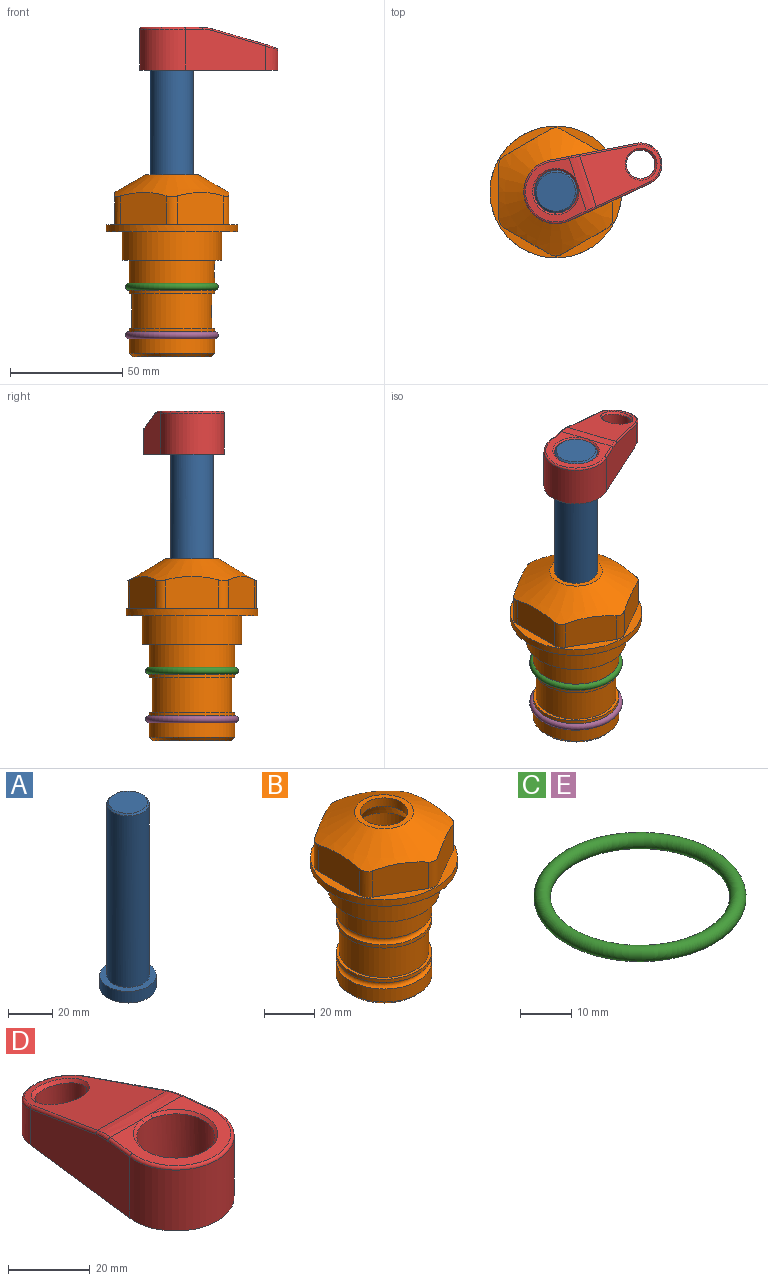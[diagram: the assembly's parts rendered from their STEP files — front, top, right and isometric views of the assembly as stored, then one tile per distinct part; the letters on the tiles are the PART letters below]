
ASSEMBLY  parts=5 mates=4
PART A: 6 faces, bbox 25.4x25.4x101.6 mm
  f0: plane 17.46x17.46mm, normal (0,0,1), area 239.5mm2, adj f5
  f1: plane 25.4x25.4mm, normal (0,0,-1), area 506.7mm2, adj f2
  f2: cylinder r=12.7mm len=25.4mm, axis (0,0,1), area 506.7mm2, adj f1,f3
  f3: plane 25.4x25.4mm, normal (0,0,1), area 221.7mm2, adj f2,f4
  f4: cylinder r=9.53mm len=94.46mm, axis (0,0,1), area 5653mm2, adj f3,f5
  f5: cone r=8.73mm half-angle=45deg, axis (0,0,-1), area 64.4mm2, adj f0,f4
PART B: 36 faces, bbox 58.7x58.7x81 mm
  f0: cylinder r=17.78mm len=35.56mm, axis (0,0,1), area 1670.8mm2, adj f23,f24,f31
  f1: cylinder r=19.05mm len=38.1mm, axis (0,0,1), area 1191.9mm2, adj f26,f27,f30
  f2: plane 58.66x58.66mm, normal (0,0,-1), area 1150.6mm2, adj f3,f28
  f3: cylinder r=29.33mm len=58.66mm, axis (0,0,-1), area 585.1mm2, adj f2,f4
  f4: plane 58.66x58.66mm, normal (0,0,1), area 475.9mm2, adj f3,f5,f6,f7,f8,f9,f10,f11
  f5: plane 20.32x14.34mm, normal (-0.5,0.87,0), area 324.4mm2, adj f4,f15,f16,f17
  f6: plane 20.32x14.34mm, normal (0.5,0.87,0), area 324.4mm2, adj f4,f14,f15,f17
  f7: plane 23.48x14.34mm, normal (1,0,0), area 324.4mm2, adj f4,f13,f14,f17
  f8: plane 20.32x14.34mm, normal (0.5,-0.87,0), area 324.4mm2, adj f4,f12,f13,f17
  f9: plane 20.32x14.34mm, normal (-0.5,-0.87,0), area 324.4mm2, adj f4,f11,f12,f17
  f10: plane 23.48x14.34mm, normal (-1,0,0), area 324.4mm2, adj f4,f11,f16,f17
  f11: cylinder r=5.08mm len=12.85mm, axis (0,0,-1), area 67.2mm2, adj f4,f9,f10,f17
  f12: cylinder r=5.08mm len=12.85mm, axis (0,0,-1), area 67.2mm2, adj f4,f8,f9,f17
  f13: cylinder r=5.08mm len=12.85mm, axis (0,0,-1), area 67.2mm2, adj f4,f7,f8,f17
  f14: cylinder r=5.08mm len=12.85mm, axis (0,0,-1), area 67.2mm2, adj f4,f6,f7,f17
  f15: cylinder r=5.08mm len=12.85mm, axis (0,0,-1), area 67.2mm2, adj f4,f5,f6,f17
  f16: cylinder r=5.08mm len=12.85mm, axis (0,0,-1), area 67.2mm2, adj f4,f5,f10,f17
  f17: cone r=11.73mm half-angle=60deg, axis (0,0,-1), area 2071.8mm2, adj f5,f6,f7,f8,f9,f10,f11,f12
  f18: plane 23.46x23.46mm, normal (0,0,1), area 147.4mm2, adj f17,f35
  f19: plane 34.93x34.93mm, normal (0,0,-1), area 958mm2, adj f29
  f20: cylinder r=19.05mm len=38.1mm, axis (0,0,1), area 760.1mm2, adj f21,f29
  f21: torus R=19.05mm, axis (0,0,1), area 565.3mm2, adj f20,f22
  f22: cylinder r=19.05mm len=38.1mm, axis (0,0,1), area 190mm2, adj f21,f23
  f23: plane 38.1x38.1mm, normal (0,0,1), area 146.9mm2, adj f0,f22
  f24: plane 38.1x38.1mm, normal (0,0,-1), area 146.9mm2, adj f0,f25
  f25: cylinder r=19.05mm len=38.1mm, axis (0,0,1), area 190mm2, adj f24,f26
  f26: torus R=19.05mm, axis (0,0,1), area 565.3mm2, adj f1,f25
  f27: plane 44.45x44.45mm, normal (0,0,-1), area 411.7mm2, adj f1,f28
  f28: cylinder r=22.23mm len=44.45mm, axis (0,0,1), area 1773.5mm2, adj f2,f27
  f29: cone r=19.05mm half-angle=45deg, axis (0,0,1), area 257.5mm2, adj f19,f20
  f30: cylinder r=3.17mm len=6.75mm, axis (-1,0,0), area 128mm2, adj f1,f33
  f31: cylinder r=3.17mm len=6.35mm, axis (-1,0,0), area 102.5mm2, adj f0,f33
  f32: plane 25.4x25.4mm, normal (0,0,1), area 506.7mm2, adj f33
  f33: cylinder r=12.7mm len=66.42mm, axis (0,0,-1), area 5236.2mm2, adj f30,f31,f32,f34
  f34: cone r=9.53mm half-angle=30deg, axis (0,0,-1), area 443.4mm2, adj f33,f35
  f35: cylinder r=9.53mm len=19.05mm, axis (0,0,-1), area 240.9mm2, adj f18,f34
PART C: 1 faces, bbox 44.7x44.7x3.2 mm
  f0: torus R=19.05mm, axis (0,0,1), area 1193.9mm2
PART D: 31 faces, bbox 31.7x65.5x19.8 mm
  f0: plane 39.12x18.26mm, normal (0.99,0.12,0), area 612.2mm2, adj f1,f4,f7,f11,f13,f15
  f1: cylinder r=9.53mm len=18.91mm, axis (0,0,-1), area 296.1mm2, adj f0,f2,f7,f17
  f2: plane 39.12x18.26mm, normal (-0.99,0.12,0), area 612.2mm2, adj f1,f4,f7,f12,f14,f16
  f3: cylinder r=6.35mm len=12.7mm, axis (0,0,-1), area 362.4mm2, adj f7,f18
  f4: cylinder r=14.29mm len=28.58mm, axis (0,0,-1), area 882.2mm2, adj f0,f2,f7,f10
  f5: cylinder r=9.53mm len=19.05mm, axis (0,0,-1), area 1092.6mm2, adj f7,f19,f20
  f6: plane 26.99x23.69mm, normal (0,0,1), area 216.2mm2, adj f9,f10,f11,f12,f19
  f7: plane 63.5x28.58mm, normal (0,0,-1), area 661.8mm2, adj f0,f1,f2,f3,f4,f5,f22,f23
  f8: plane 33.52x23.6mm, normal (0,0.26,0.97), area 486mm2, adj f9,f15,f16,f17,f18
  f9: cylinder r=19.05mm len=24.72mm, axis (1,0,0), area 120.4mm2, adj f6,f8,f13,f14,f20
  f10: torus R=13.49mm, axis (0,0,1), area 59mm2, adj f4,f6,f11,f12
  f11: cylinder r=0.79mm len=8.67mm, axis (0.12,-0.99,0), area 10.8mm2, adj f0,f6,f10,f13
  f12: cylinder r=0.79mm len=8.67mm, axis (0.12,0.99,0), area 10.8mm2, adj f2,f6,f10,f14
  f13: bspline ~4.95x1.42mm, area 6.1mm2, adj f0,f9,f11,f15
  f14: bspline ~4.95x1.42mm, area 6.1mm2, adj f2,f9,f12,f16
  f15: cylinder r=0.79mm len=25.95mm, axis (0.12,-0.96,0.26), area 32.9mm2, adj f0,f8,f13,f17
  f16: cylinder r=0.79mm len=25.95mm, axis (0.12,0.96,-0.26), area 32.9mm2, adj f2,f8,f14,f17
  f17: bspline ~18.91x8.38mm, area 30mm2, adj f1,f8,f15,f16
  f18: bspline ~14.29x14.29mm, area 48.3mm2, adj f3,f8
  f19: cone r=9.53mm half-angle=45deg, axis (0,0,1), area 66.5mm2, adj f5,f6,f20
  f20: bspline ~3.22x0.96mm, area 3.5mm2, adj f5,f9,f19
  f21: plane 2.75x2.72mm, normal (0,0,-1), area 2.9mm2, adj f23,f25,f28
  f22: plane 23.05x15.88mm, normal (-0.99,-0.12,0), area 323.6mm2, adj f7,f25,f26,f27,f28,f29
  f23: plane 23.05x15.88mm, normal (0.99,-0.12,0), area 323.6mm2, adj f7,f21,f25,f27,f28,f30
  f24: cylinder r=9.53mm len=10.69mm, axis (0,0,-1), area 114.7mm2, adj f7,f27,f29,f30
  f25: cylinder r=12.7mm len=20.59mm, axis (0,0,-1), area 381.1mm2, adj f7,f21,f22,f23,f26,f28
  f26: plane 2.75x2.72mm, normal (0,0,-1), area 2.9mm2, adj f22,f25,f28
  f27: plane 19.72x18.37mm, normal (0,-0.26,-0.97), area 291.8mm2, adj f22,f23,f24,f28,f29,f30
  f28: cylinder r=15.88mm len=19.92mm, axis (1,0,0), area 54.8mm2, adj f21,f22,f23,f25,f26,f27
  f29: cylinder r=1.59mm len=11mm, axis (0,0,-1), area 34.7mm2, adj f7,f22,f24,f27
  f30: cylinder r=1.59mm len=11mm, axis (0,0,-1), area 34.7mm2, adj f7,f23,f24,f27
PART E: same geometry as C
PLACE A rot(axis=(0,0,-1),72.1deg) t=(0,0,27.55)mm
PLACE B at identity fixed
PLACE C at identity
PLACE D rot(axis=(0,0,-1),72.1deg) t=(0,0,27.55)mm
PLACE E t=(0,0,-21.59)mm
MATE cylindrical A.f2 <-> B.f0  axis (0,0,-1) through (0,0,-10.55)mm
MATE fastened E.f0 <-> B.f0  axis (0,0,1) through (0,0,-46.1)mm
MATE fastened C.f0 <-> B.f0  axis (0,0,1) through (0,0,-24.51)mm
MATE fastened D.f4 <-> A.f2  axis (0,0,1) through (0,0,91.05)mm
